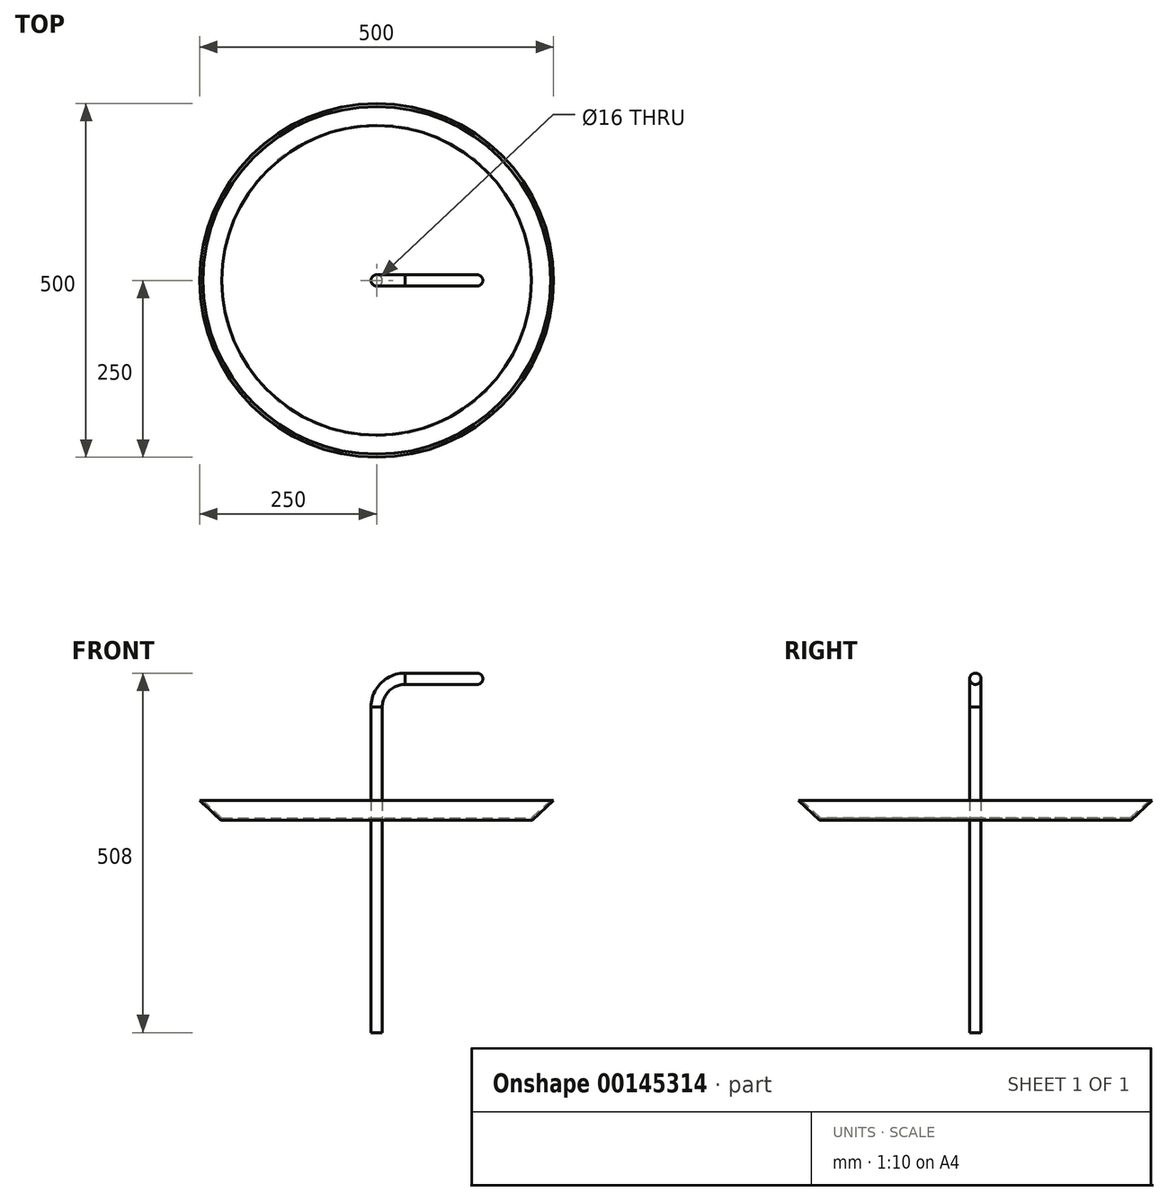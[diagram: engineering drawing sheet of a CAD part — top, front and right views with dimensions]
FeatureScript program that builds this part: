
annotation { "Feature Type Name" : "Feature", "Feature Type Description" : "" }
export const myFeature = defineFeature(function(context is Context, id is Id, definition is map)
    precondition{}
    {
        {
            var Q0;
            Q0=qCreatedBy(makeId("Front.planeOp"),FACE);
            var sketch = newSketch(context, id + "F0", { "sketchPlane" : qUnion([Q0])});
            skLineSegment(sketch, "E0", {"start": v(0, 0) * mm, "end": v(0, 460) * mm});
            skArc(sketch, "E1", {"start": v(0, 460) * mm, "mid": v(11.72, 488.28) * mm, "end": v(40, 500) * mm});
            skLineSegment(sketch, "E2", {"start": v(40, 500) * mm, "end": v(142, 500) * mm});
            skLineSegment(sketch, "E3.0", {"start": v(40, 492) * mm, "end": v(142, 492) * mm});
            skArc(sketch, "E3.1", {"start": v(8, 460) * mm, "mid": v(17.37, 482.63) * mm, "end": v(40, 492) * mm});
            skLineSegment(sketch, "E3.2", {"start": v(8, 0) * mm, "end": v(8, 460) * mm});
            skArc(sketch, "E4", {"start": v(142, 492) * mm, "mid": v(147.66, 494.34) * mm, "end": v(150, 500) * mm});
            skLineSegment(sketch, "E5", {"start": v(142, 500) * mm, "end": v(150, 500) * mm});
            skLineSegment(sketch, "E6", {"start": v(0, 300) * mm, "end": v(220, 300) * mm});
            skLineSegment(sketch, "E7", {"start": v(220, 300) * mm, "end": v(250, 328.17) * mm});
            skLineSegment(sketch, "E8", {"start": v(250, 328.17) * mm, "end": v(245.62, 328.17) * mm});
            skLineSegment(sketch, "E9", {"start": v(245.62, 328.17) * mm, "end": v(218.81, 303) * mm});
            skLineSegment(sketch, "E10", {"start": v(0, 303) * mm, "end": v(218.81, 303) * mm});
            skLineSegment(sketch, "E11", {"start": v(8, 0) * mm, "end": v(0, 0) * mm});
            skLineSegment(sketch, "E12", {"start": v(0, 460) * mm, "end": v(8, 460) * mm});
            skLineSegment(sketch, "E13", {"start": v(40, 500) * mm, "end": v(40, 492) * mm});
            skSolve(sketch);
        }
        {
            var Q0;
            {var subQ0=sQuery(id+"F0.wireOp",EDGE,"E7");Q0=makeQuery(id+"F0.imprint","IMPRINT",FACE,{"disambiguationData":[TD([[makeQuery(id+"F0.imprint","IMPRINT",EDGE,{"derivedFrom":subQ0}),1.0]])]});}
            var Q1;
            Q1=sQuery(id+"F0.wireOp",EDGE,"E0");
            revolve(context, id + "F1", {"entities" : qUnion([Q0]), "axis" : qUnion([Q1]), "revolveType" : RevolveType.FULL});
        }
        {
            var Q0;
            {var subQ0=sQuery(id+"F0.wireOp",EDGE,"E12");Q0=makeQuery(id+"F0.imprint","IMPRINT",FACE,{"disambiguationData":[TD([[makeQuery(id+"F0.imprint","IMPRINT",EDGE,{"derivedFrom":subQ0}),-1.0]])]});}
            var Q1;
            Q1=sQuery(id+"F0.wireOp",EDGE,"E0");
            revolve(context, id + "F2", {"entities" : qUnion([Q0]), "axis" : qUnion([Q1]), "revolveType" : RevolveType.FULL});
        }
        {
            var Q0;
            Q0=makeQuery(id+"F0.imprint","IMPRINT",FACE,{"disambiguationData":[TD([[makeQuery(id+"F0.imprint","IMPRINT",EDGE,{"derivedFrom":sQuery(id+"F0.wireOp",EDGE,"E2")}),-1.0]])]});
            var Q1;
            Q1=sQuery(id+"F0.wireOp",EDGE,"E2");
            revolve(context, id + "F3", {"entities" : qUnion([Q0]), "axis" : qUnion([Q1]), "revolveType" : RevolveType.FULL});
        }
        {
            var Q0;
            {var subQ0=sQuery(id+"F0.wireOp",EDGE,"E11");Q0=makeQuery(id+"F0.imprint","IMPRINT",FACE,{"disambiguationData":[TD([[makeQuery(id+"F0.imprint","IMPRINT",EDGE,{"derivedFrom":subQ0}),-1.0]])]});}
            var Q1;
            Q1=sQuery(id+"F0.wireOp",EDGE,"E0");
            revolve(context, id + "F4", {"entities" : qUnion([Q0]), "axis" : qUnion([Q1]), "revolveType" : RevolveType.FULL});
        }
        {
            var Q0;
            Q0=makeQuery(id+"F2.opRevolve","SWEPT_FACE",FACE,{"disambiguationData":[OSD([sQuery(id+"F0.wireOp",EDGE,"E12")])]});
            var Q1;
            Q1=sQuery(id+"F0.wireOp",EDGE,"E1");
            sweep(context, id + "F5", {"profiles" : qUnion([Q0]), "path" : qUnion([Q1])});
        }
    });
